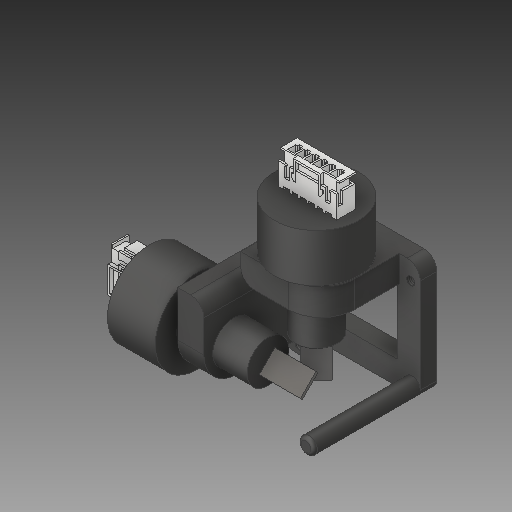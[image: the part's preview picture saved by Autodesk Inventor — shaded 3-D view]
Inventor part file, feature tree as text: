
AUTODESK INVENTOR PART (.ipt)
format: ipt  version: 2017 (Build 210142000, 142)  size: 1,176,064 bytes
history: native  units: mm
features: sketch x16, extrude x12, other x7, projected_geometry x6, fillet x2, hole x1
ambient origin geometry x8: Origin, YZ Plane, XZ Plane, XY Plane, X Axis, Y Axis, Z Axis, Center Point
bodies: Solide1 (feature_tree), Solide2 (feature_tree), Solide3 (feature_tree)
feature tree (44):
  other  "Connecteur jst 6 broches.iam"
  other  "Connecteur jst 6 broches femelle.ipt:1"
  other  "Connecteur JST 6 Broches Male.ipt:1"
  extrude  "Extrusion1"  Depth=41.95mm
  extrude  "Extrusion2"  Depth=35.16mm
  extrude  "Extrusion3"  Depth=10.0mm
  fillet  "Congé2"  Radius=6.5mm
  extrude  "Extrusion4"  Depth=2.5mm
  fillet  "Congé3"  Radius=4.0mm
  hole  "Perçage1"  [1 undecoded]
  extrude  "Extrusion5"  Depth=20.0mm
  extrude  "Extrusion6"  Depth=7.0mm
  extrude  "Extrusion7"  Depth=8.0mm
  extrude  "Extrusion8"  Depth=5.0mm TaperAngle=0.0deg
  extrude  "Extrusion9"  Depth=24.5mm
  extrude  "Extrusion10"  Depth=11.0mm
  extrude  "Extrusion11"  Depth=23.5mm TaperAngle=0.0deg
  extrude  "Extrusion12"  Depth=23.8mm
  sketch  "Esquisse17"
  other  "Plan de construction2"
  other  "Déplacer des corps1"
  other  "Déplacer des corps2"
  other  "Combiner1"
  sketch  "Esquisse18"
  sketch  "Esquisse19"
  sketch  "Esquisse1"
  sketch  "Esquisse2"
  sketch  "Esquisse3"
  sketch  "Esquisse4"
  projected_geometry  "Boucle projetée1"
  sketch  "Esquisse5"
  sketch  "Esquisse6"
  sketch  "Esquisse7"
  sketch  "Esquisse8"
  projected_geometry  "Boucle projetée2"
  sketch  "Esquisse9"
  sketch  "Esquisse10"
  projected_geometry  "Boucle projetée3"
  sketch  "Esquisse11"
  projected_geometry  "Boucle projetée4"
  sketch  "Esquisse12"
  projected_geometry  "Boucle projetée5"
  sketch  "Esquisse13"
  projected_geometry  "Boucle projetée6"
note: 1 required parameter value undecoded (feature->parameter linkage not recoverable at this tier; creation-order binding heuristic only, values carry confidence <= 0.55)
